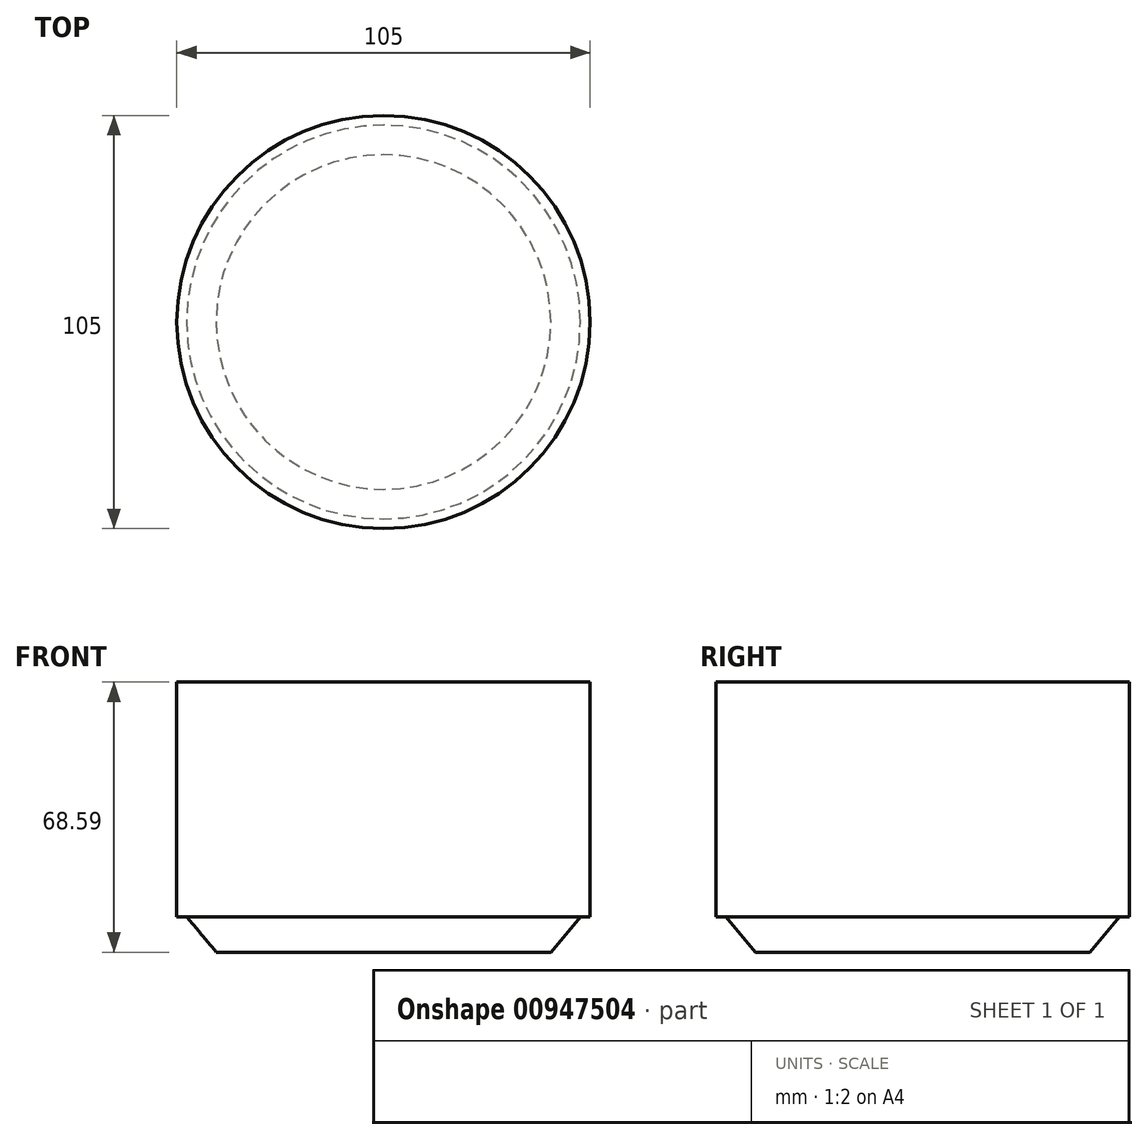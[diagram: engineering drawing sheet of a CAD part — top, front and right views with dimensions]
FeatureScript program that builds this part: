
annotation { "Feature Type Name" : "Feature", "Feature Type Description" : "" }
export const myFeature = defineFeature(function(context is Context, id is Id, definition is map)
    precondition{}
    {
        {
            var Q0;
            Q0=qCreatedBy(makeId("Front.planeOp"),FACE);
            var sketch = newSketch(context, id + "F0", { "sketchPlane" : qUnion([Q0])});
            skLineSegment(sketch, "E0", {"start": v(0, 0) * mm, "end": v(0, 68.6) * mm});
            skLineSegment(sketch, "E1", {"start": v(0, 0) * mm, "end": v(42.5, 0) * mm});
            skLineSegment(sketch, "E2", {"start": v(0, 9) * mm, "end": v(52.5, 9) * mm});
            skLineSegment(sketch, "E3", {"start": v(0, 9) * mm, "end": v(50, 9) * mm});
            skLineSegment(sketch, "E4", {"start": v(50, 9) * mm, "end": v(42.5, 0) * mm});
            skLineSegment(sketch, "E5", {"start": v(0, 68.6) * mm, "end": v(52.5, 68.6) * mm});
            skLineSegment(sketch, "E6", {"start": v(52.5, 68.59) * mm, "end": v(52.5, 9) * mm});
            skSolve(sketch);
        }
        {
            var Q0;
            Q0=makeQuery(id+"F0.imprint","IMPRINT",FACE,{"disambiguationData":[TD([[makeQuery(id+"F0.imprint","IMPRINT",EDGE,{"derivedFrom":sQuery(id+"F0.wireOp",EDGE,"E2")}),1.0]])]});
            var Q1;
            {var subQ0=sQuery(id+"F0.wireOp",EDGE,"E1");Q1=makeQuery(id+"F0.imprint","IMPRINT",FACE,{"disambiguationData":[TD([[makeQuery(id+"F0.imprint","IMPRINT",EDGE,{"derivedFrom":subQ0}),1.0]])]});}
            var Q2;
            Q2=sQuery(id+"F0.wireOp",EDGE,"E0");
            revolve(context, id + "F1", {"surfaceOperationType" : NewSurfaceOperationType.NEW, "entities" : qUnion([Q0, Q1]), "axis" : qUnion([Q2]), "revolveType" : RevolveType.FULL});
        }
    });
